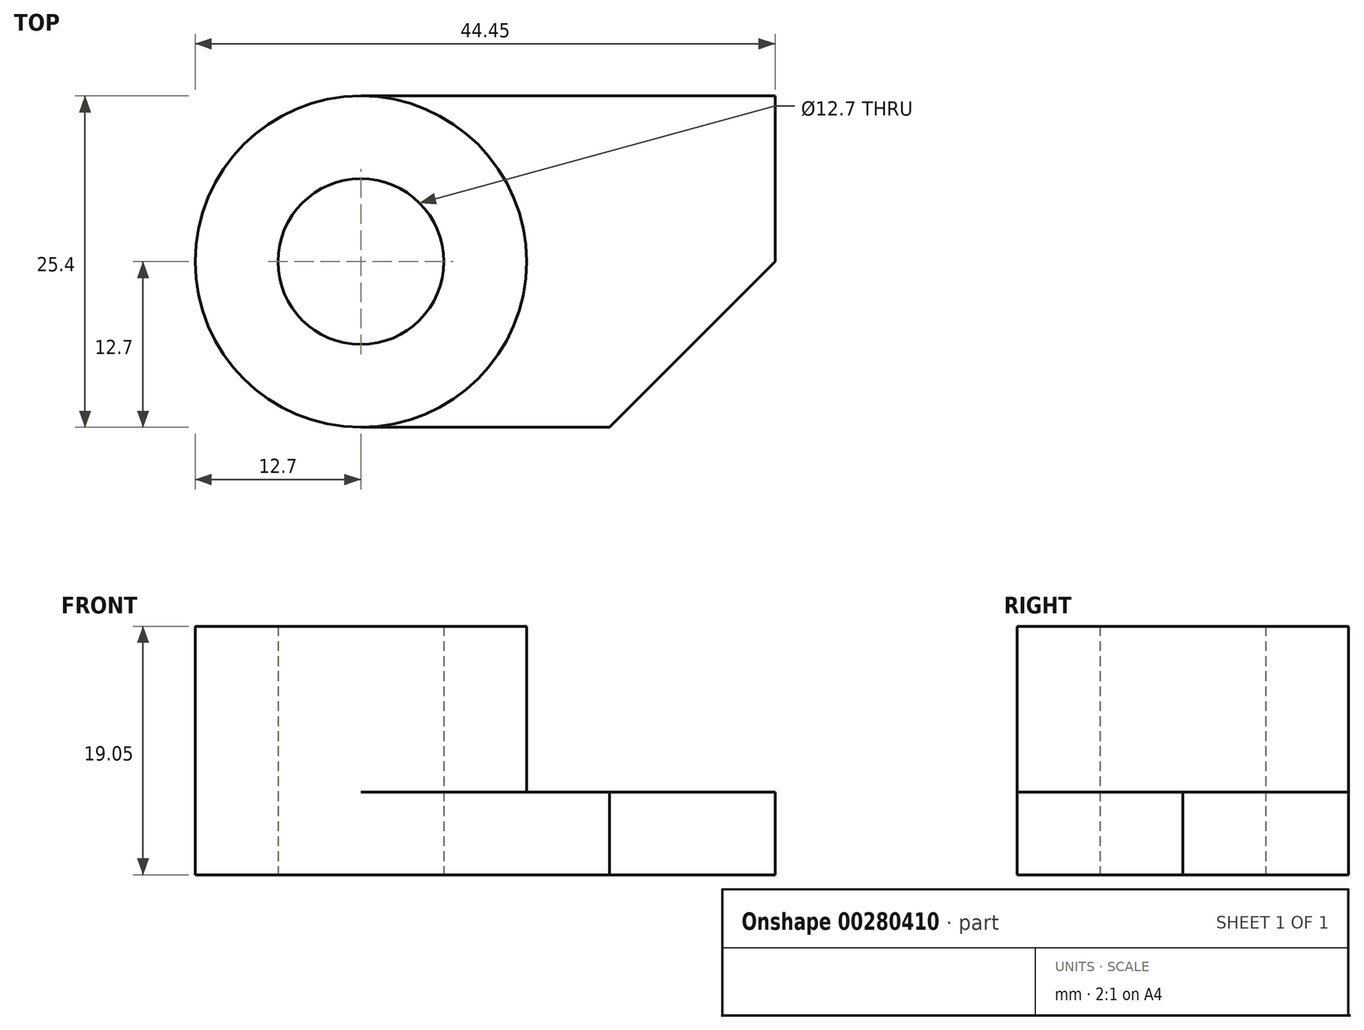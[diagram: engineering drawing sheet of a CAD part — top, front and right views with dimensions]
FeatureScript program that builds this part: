
annotation { "Feature Type Name" : "Feature", "Feature Type Description" : "" }
export const myFeature = defineFeature(function(context is Context, id is Id, definition is map)
    precondition{}
    {
        {
            var Q0;
            Q0=qCreatedBy(makeId("Top.planeOp"),FACE);
            var sketch = newSketch(context, id + "F0", { "sketchPlane" : qUnion([Q0])});
            skCircle(sketch, "E0", {"center": v(0, 0) * mm, "radius": 12.7 * mm});
            skCircle(sketch, "E1", {"center": v(0, 0) * mm, "radius": 6.35 * mm});
            skSolve(sketch);
        }
        {
            var Q0;
            Q0=makeQuery(id+"F0.imprint","IMPRINT",FACE,{"disambiguationData":[TD([[makeQuery(id+"F0.imprint","IMPRINT",EDGE,{"derivedFrom":sQuery(id+"F0.wireOp",EDGE,"E0")}),1.0]])]});
            extrude(context, id + "F1", {"entities" : qUnion([Q0]), "depth" : 19.05 * mm});
        }
        {
            var Q0;
            Q0=qCreatedBy(makeId("Top.planeOp"),FACE);
            var sketch = newSketch(context, id + "F2", { "sketchPlane" : qUnion([Q0])});
            skLineSegment(sketch, "E2", {"start": v(0, 12.7) * mm, "end": v(31.75, 12.7) * mm});
            skLineSegment(sketch, "E3", {"start": v(31.75, 12.7) * mm, "end": v(31.75, -12.7) * mm});
            skLineSegment(sketch, "E4", {"start": v(31.75, -12.7) * mm, "end": v(0, -12.7) * mm});
            skLineSegment(sketch, "E5", {"start": v(0, -12.7) * mm, "end": v(0, 12.7) * mm});
            skSolve(sketch);
        }
        {
            var Q0;
            Q0 = qSketchRegion(id + "F2", true);
            extrude(context, id + "F3", {"entities" : qUnion([Q0]), "operationType" : NewBodyOperationType.ADD, "depth" : 6.35 * mm});
        }
        {
            var Q0;
            {var subQ0=sQuery(id+"F2.wireOp",EDGE,"E5");Q0=makeQuery(id+"F3.boolean.opBoolean","SPLIT",FACE,{"disambiguationData":[TD([makeQuery(id+"F1.opExtrude","SWEPT_FACE",FACE,{"disambiguationData":[OSD([sQuery(id+"F0.wireOp",EDGE,"E1")])]})])],"derivedFrom":makeQuery(id+"F3.opExtrude","CAP_FACE",FACE,{"disambiguationData":[OSD([sQuery(id+"F2.wireOp",EDGE,"E2"),sQuery(id+"F2.wireOp",EDGE,"E3"),sQuery(id+"F2.wireOp",EDGE,"E4"),subQ0])],"isStart":false})});}
            extrude(context, id + "F4", {"entities" : qUnion([Q0]), "operationType" : NewBodyOperationType.REMOVE, "oppositeDirection" : true, "depth" : 25.4 * mm});
        }
        {
            var Q0;
            {var subQ0=sQuery(id+"F2.wireOp",EDGE,"E2");var subQ1=sQuery(id+"F2.wireOp",EDGE,"E3");var subQ2=sQuery(id+"F2.wireOp",EDGE,"E4");Q0=makeQuery(id+"F3.boolean.opBoolean","SPLIT",FACE,{"disambiguationData":[TD([makeQuery(id+"F1.opExtrude","SWEPT_FACE",FACE,{"disambiguationData":[OSD([sQuery(id+"F0.wireOp",EDGE,"E0")])]})])],"derivedFrom":makeQuery(id+"F3.opExtrude","CAP_FACE",FACE,{"disambiguationData":[OSD([subQ0,subQ1,subQ2,sQuery(id+"F2.wireOp",EDGE,"E5")])],"isStart":false})});}
            var sketch = newSketch(context, id + "F5", { "sketchPlane" : qUnion([Q0])});
            skLineSegment(sketch, "E6", {"start": v(31.75, 0) * mm, "end": v(19.05, -12.7) * mm});
            skLineSegment(sketch, "E7", {"start": v(19.05, -12.7) * mm, "end": v(31.75, -12.7) * mm});
            skLineSegment(sketch, "E8", {"start": v(31.75, -12.7) * mm, "end": v(31.75, 0) * mm});
            skSolve(sketch);
        }
        {
            var Q0;
            Q0=makeQuery(id+"F5.imprint","IMPRINT",FACE,{"disambiguationData":[TD([[makeQuery(id+"F5.imprint","IMPRINT",EDGE,{"derivedFrom":sQuery(id+"F5.wireOp",EDGE,"E6")}),1.0]])]});
            extrude(context, id + "F6", {"entities" : qUnion([Q0]), "operationType" : NewBodyOperationType.REMOVE, "oppositeDirection" : true, "depth" : 25.4 * mm});
        }
    });
